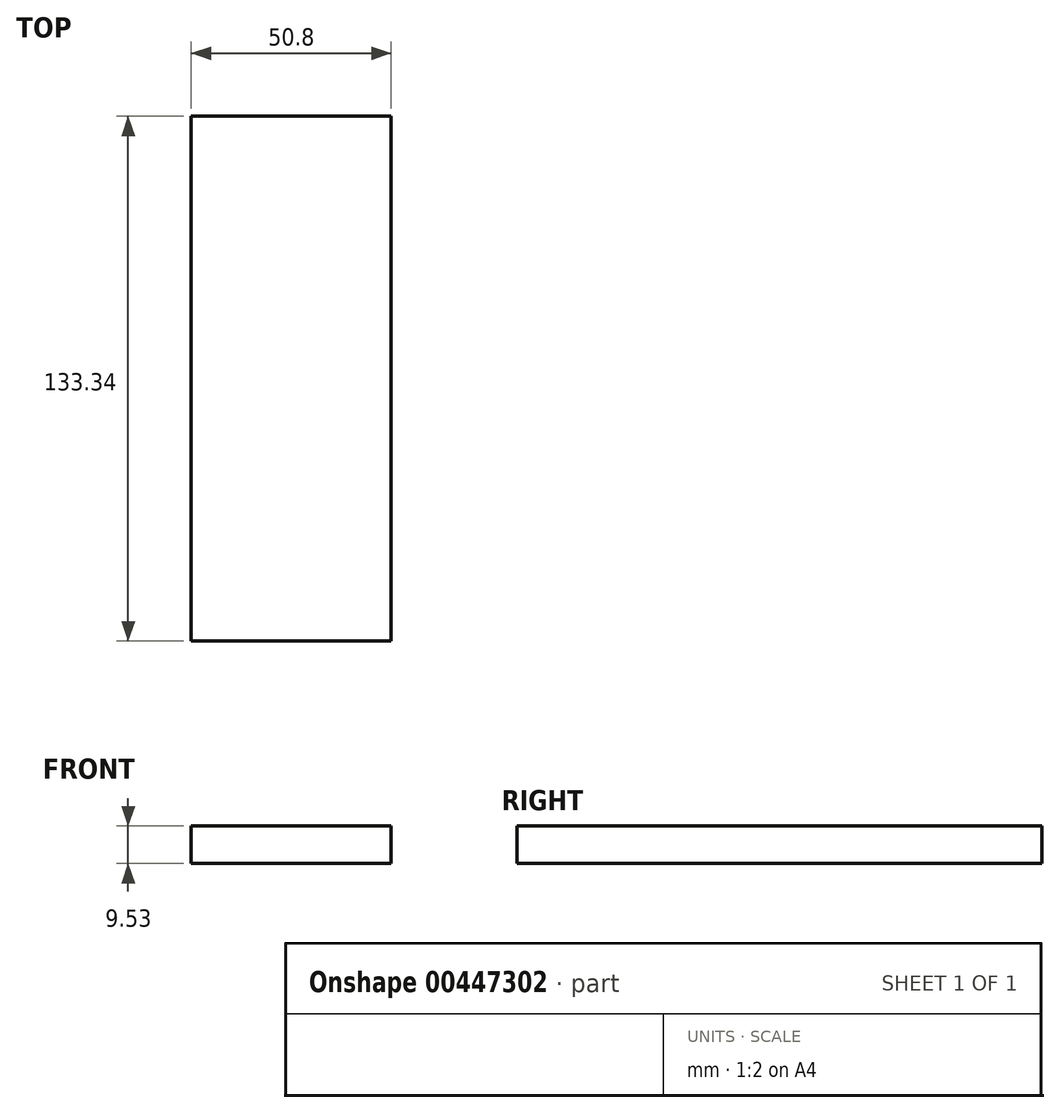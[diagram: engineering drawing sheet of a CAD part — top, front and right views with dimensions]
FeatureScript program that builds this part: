
annotation { "Feature Type Name" : "Feature", "Feature Type Description" : "" }
export const myFeature = defineFeature(function(context is Context, id is Id, definition is map)
    precondition{}
    {
        {
            var Q0;
            Q0=qCreatedBy(makeId("Top.planeOp"),FACE);
            var sketch = newSketch(context, id + "F0", { "sketchPlane" : qUnion([Q0])});
            skLineSegment(sketch, "E0.bottom", {"start": v(-25.4, 66.68) * mm, "end": v(25.4, 66.68) * mm});
            skLineSegment(sketch, "E0.top", {"start": v(-25.4, -66.68) * mm, "end": v(25.4, -66.68) * mm});
            skLineSegment(sketch, "E0.left", {"start": v(-25.4, 66.68) * mm, "end": v(-25.4, -66.68) * mm});
            skLineSegment(sketch, "E0.right", {"start": v(25.4, 66.68) * mm, "end": v(25.4, -66.68) * mm});
            skPoint(sketch, "E0.middle", {"position": v(0, 0) * mm});
            skSolve(sketch);
        }
        {
            var Q0;
            Q0=makeQuery(id+"F0.imprint","IMPRINT",FACE,{"disambiguationData":[TD([[makeQuery(id+"F0.imprint","IMPRINT",EDGE,{"derivedFrom":sQuery(id+"F0.wireOp",EDGE,"E0.bottom")}),-1.0]])]});
            extrude(context, id + "F1", {"entities" : qUnion([Q0]), "depth" : 9.52 * mm});
        }
    });
